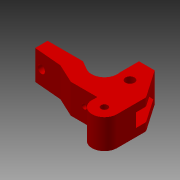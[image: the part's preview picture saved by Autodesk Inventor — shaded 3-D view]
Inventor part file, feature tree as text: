
AUTODESK INVENTOR PART (.ipt)
format: ipt  version: 2013 (Build 170138000, 138)  size: 230,912 bytes
history: native  units: mm
features: extrude x5, sketch x5, projected_geometry x3
ambient origin geometry x8: Origin, YZ Plane, XZ Plane, XY Plane, X Axis, Y Axis, Z Axis, Center Point
bodies: Solid1 (feature_tree)
feature tree (13):
  extrude  "Extrusion1"  Depth=9.5mm TaperAngle=0.0deg
  extrude  "Extrusion2"  Depth=15.0mm
  extrude  "Extrusion3"  Depth=3.5mm
  extrude  "Extrusion4"  Depth=26.8mm
  extrude  "Extrusion5"  Depth=12.0mm TaperAngle=0.0deg
  sketch  "Sketch1"  dims[d0=3.5mm d1=0.0mm d2=9.5mm d3=0.0mm]
  sketch  "Sketch4"  dims[d4=3.5mm d5=0.0mm d6=15.0mm]
  sketch  "Sketch5"  dims[d8=3.5mm d9=0.0mm d10=3.5mm]
  projected_geometry  "Projected Loop1"
  projected_geometry  "Projected Loop2"
  projected_geometry  "Projected Loop3"
  sketch  "Sketch6"  dims[d13=6.5mm d14=26.8mm]
  sketch  "Sketch7"  dims[d15=2.2mm d16=12.0mm d17=0.0mm]
